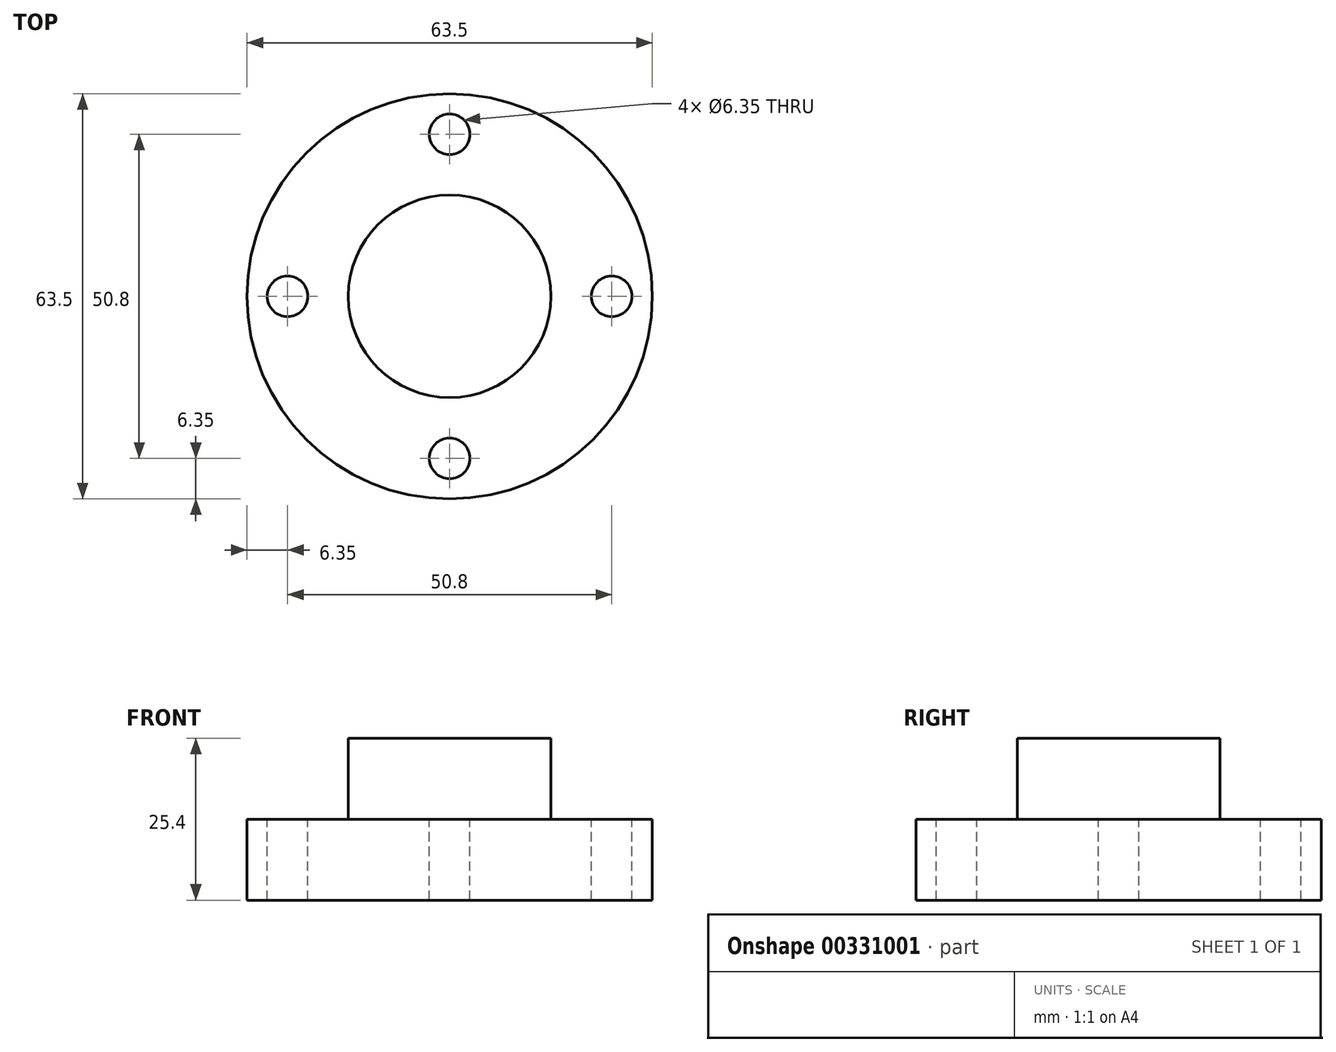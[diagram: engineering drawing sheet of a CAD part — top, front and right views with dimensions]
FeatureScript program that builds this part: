
annotation { "Feature Type Name" : "Feature", "Feature Type Description" : "" }
export const myFeature = defineFeature(function(context is Context, id is Id, definition is map)
    precondition{}
    {
        {
            var Q0;
            Q0=qCreatedBy(makeId("Top.planeOp"),FACE);
            var sketch = newSketch(context, id + "F0", { "sketchPlane" : qUnion([Q0])});
            skCircle(sketch, "E0", {"center": v(0, 0) * mm, "radius": 31.75 * mm});
            skSolve(sketch);
        }
        {
            var Q0;
            Q0 = qSketchRegion(id + "F0", true);
            extrude(context, id + "F1", {"entities" : qUnion([Q0]), "depth" : 12.7 * mm});
        }
        {
            var Q0;
            Q0=makeQuery(id+"F1.opExtrude","CAP_FACE",FACE,{"disambiguationData":[OSD([sQuery(id+"F0.wireOp",EDGE,"E0")])],"isStart":false});
            var sketch = newSketch(context, id + "F2", { "sketchPlane" : qUnion([Q0])});
            skCircle(sketch, "E1", {"center": v(0, 0) * mm, "radius": 15.88 * mm});
            skSolve(sketch);
        }
        {
            var Q0;
            Q0 = qSketchRegion(id + "F2", true);
            extrude(context, id + "F3", {"entities" : qUnion([Q0]), "operationType" : NewBodyOperationType.ADD, "depth" : 12.7 * mm});
        }
        {
            var Q0;
            Q0=makeQuery(id+"F1.opExtrude","CAP_FACE",FACE,{"disambiguationData":[OSD([sQuery(id+"F0.wireOp",EDGE,"E0")])],"isStart":false});
            var sketch = newSketch(context, id + "F4", { "sketchPlane" : qUnion([Q0])});
            skCircle(sketch, "E2", {"center": v(25.4, 0) * mm, "radius": 3.18 * mm});
            skCircle(sketch, "E3", {"center": v(0, 25.4) * mm, "radius": 3.18 * mm});
            skCircle(sketch, "E4", {"center": v(-25.4, 0) * mm, "radius": 3.18 * mm});
            skCircle(sketch, "E5", {"center": v(0, -25.4) * mm, "radius": 3.18 * mm});
            skSolve(sketch);
        }
        {
            var Q0;
            Q0 = qSketchRegion(id + "F4", true);
            extrude(context, id + "F5", {"entities" : qUnion([Q0]), "operationType" : NewBodyOperationType.REMOVE, "endBound" : BoundingType.THROUGH_ALL, "oppositeDirection" : true, "depth" : 25.4 * mm});
        }
    });
